# Revit family: KEUCO_14973010000
name_source: partatom
category: Sonderausstattung
revit_build: Autodesk Revit 2016 (Build: 20150220_1215(x64)
units: mm (PartAtom-declared; Revit-internal decimal feet)

## family parameters
Arbeitsebenenbasiert = Nein
Beim Laden mit Abzugskörper schneiden = Nein
Bemaßung runder Anschluss = Durchmesser verwenden
Gemeinsam genutzt = Nein
Immer vertikal = Ja
Raumberechnungspunkt = Nein
Teiletyp = Normal

## types (3) — shared parameters
Beschreibung = mit Ablage, offene Form
für Rollenbreite 100/120 mm
mit Antirutscheinlage in grau
Hersteller = KEUCO
Kategorie = ACC
Preisgruppe = 1
Serie = Plan
URL = https://www.keuco.com
Verwendung = GWC / WC

## per-type parameters (varying)
| type | Ausschreibungstext | Gewicht |
| 14973010000 | KEUCO PLAN Toilettenpapierhalter mit Ablage 14973010000
Hochglanzverchromter Toilettenpapierhalter, für Rollenbreite 100/120 mm, 
Ablagemöglichkeit mit grauer Antirutscheinlage aus Kautschuk, 
z.B. für  Handys und Accessoires,
in ästhetischem, funktionalem Design, offene Ausführung,
Breite 133 mm, Höhe 106 mm, Ausladung 105mm
der Toilettenpapierhalter wird verdeckt angebracht
Lieferung inkl. korrosionsfreiem Befestigungsmaterial | 670 |
| 14973070000 | KEUCO PLAN Toilettenpapierhalter mit Ablage 14973070000
Toilettenpapierhalter in Edelstahl-finish, 
für Rollenbreite 100/120 mm, 
Ablagemöglichkeit mit grauer Antirutscheinlage aus Kautschuk, 
z.B. für  Handys und Accessoires,
in ästhetischem, funktionalem Design, offene Ausführung,
Breite 133 mm, Höhe 106 mm, Ausladung 105mm
der Toilettenpapierhalter wird verdeckt angebracht
Lieferung inkl. korrosionsfreiem Befestigungsmaterial | 644.6 |
| 14973170000 | KEUCO PLAN Toilettenpapierhalter mit Ablage 14973070000
Toilettenpapierhalter silber-eloxiert/verchromt, 
für Rollenbreite 100/120 mm, 
Ablagemöglichkeit mit grauer Antirutscheinlage aus Kautschuk, 
z.B. für  Handys und Accessoires,
in ästhetischem, funktionalem Design, offene Ausführung,
Breite 133 mm, Höhe 106 mm, Ausladung 105mm
der Toilettenpapierhalter wird verdeckt angebracht
Lieferung inkl. korrosionsfreiem Befestigungsmaterial | 644.6 |

note: column(s) folded — value = type name in every type: Artikelnummer

## geometry (parser evidence)
native form markers: Blend x4, Sweep x2
no freeform markers — native parametric forms only
